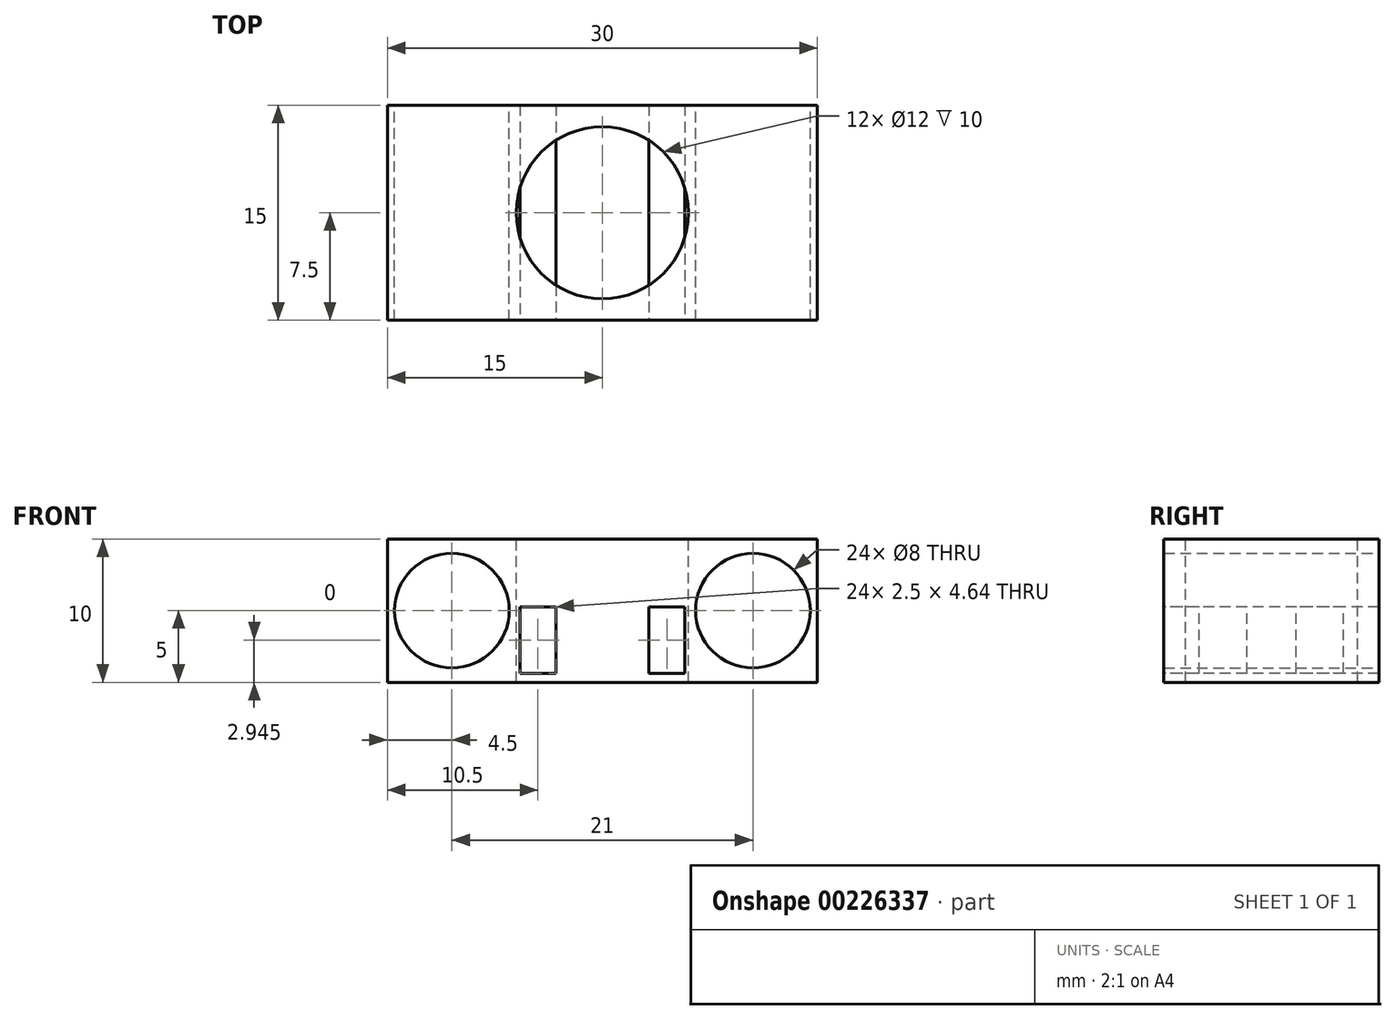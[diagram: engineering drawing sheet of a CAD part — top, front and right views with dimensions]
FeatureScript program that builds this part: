
annotation { "Feature Type Name" : "Feature", "Feature Type Description" : "" }
export const myFeature = defineFeature(function(context is Context, id is Id, definition is map)
    precondition{}
    {
        {
            var Q0;
            Q0=qCreatedBy(makeId("Front.planeOp"),FACE);
            var sketch = newSketch(context, id + "F0", { "sketchPlane" : qUnion([Q0])});
            skLineSegment(sketch, "E0.bottom", {"start": v(15, -5) * mm, "end": v(-15, -5) * mm});
            skLineSegment(sketch, "E0.top", {"start": v(15, 5) * mm, "end": v(-15, 5) * mm});
            skLineSegment(sketch, "E0.left", {"start": v(15, -5) * mm, "end": v(15, 5) * mm});
            skLineSegment(sketch, "E0.right", {"start": v(-15, -5) * mm, "end": v(-15, 5) * mm});
            skPoint(sketch, "E0.middle", {"position": v(0, 0) * mm});
            skCircle(sketch, "E1", {"center": v(10.5, 0) * mm, "radius": 4 * mm});
            skCircle(sketch, "E2", {"center": v(-10.5, 0) * mm, "radius": 4 * mm});
            skPoint(sketch, "E3.orphan", {"position": v(21, 0) * mm});
            skLineSegment(sketch, "E4", {"start": v(-10.5, 0) * mm, "end": v(-6.5, 0) * mm});
            skLineSegment(sketch, "E5", {"start": v(-6.5, 0) * mm, "end": v(0, 0) * mm});
            skLineSegment(sketch, "E6", {"start": v(0, 0) * mm, "end": v(6.5, 0) * mm});
            skLineSegment(sketch, "E7", {"start": v(6.5, 0) * mm, "end": v(10.05, 0) * mm});
            skLineSegment(sketch, "E8.bottom", {"start": v(6, -0.68) * mm, "end": v(-6, -0.68) * mm});
            skLineSegment(sketch, "E8.top", {"start": v(6, 0.68) * mm, "end": v(-6, 0.68) * mm});
            skLineSegment(sketch, "E8.left", {"start": v(6, -0.68) * mm, "end": v(6, 0.68) * mm});
            skLineSegment(sketch, "E8.right", {"start": v(-6, -0.68) * mm, "end": v(-6, 0.68) * mm});
            skSolve(sketch);
        }
        {
            var Q0;
            Q0 = qSketchRegion(id + "F0", true);
            var Q1;
            {var subQ1=sQuery(id+"F0.wireOp",EDGE,"E8.bottom");Q1=makeQuery(id+"F0.imprint","IMPRINT",FACE,{"disambiguationData":[TD([[makeQuery(id+"F0.imprint","IMPRINT",EDGE,{"derivedFrom":subQ1}),-1.0]])]});}
            var Q2;
            {var subQ1=sQuery(id+"F0.wireOp",EDGE,"E8.top");Q2=makeQuery(id+"F0.imprint","IMPRINT",FACE,{"disambiguationData":[TD([[makeQuery(id+"F0.imprint","IMPRINT",EDGE,{"derivedFrom":subQ1}),1.0]])]});}
            extrude(context, id + "F1", {"entities" : qUnion([Q0, Q1, Q2]), "depth" : 15 * mm});
        }
        {
            var Q0;
            Q0=makeQuery(id+"F1.opExtrude","SWEPT_FACE",FACE,{"disambiguationData":[OSD([sQuery(id+"F0.wireOp",EDGE,"E0.top")])]});
            var sketch = newSketch(context, id + "F2", { "sketchPlane" : qUnion([Q0])});
            skLineSegment(sketch, "E9", {"start": v(-15, -7.5) * mm, "end": v(15, -7.5) * mm});
            skCircle(sketch, "E10", {"center": v(0, -7.5) * mm, "radius": 6 * mm});
            skSolve(sketch);
        }
        {
            var Q0;
            Q0=sQuery(id+"F2.wireOp",VERTEX,"E10.center");
            var Q1;
            Q1=makeQuery(id+"F1.opExtrude","SWEPT_BODY",BODY,{"disambiguationData":[OSD([sQuery(id+"F0.wireOp",EDGE,"E0.bottom"),sQuery(id+"F0.wireOp",EDGE,"E0.top"),sQuery(id+"F0.wireOp",EDGE,"E0.left"),sQuery(id+"F0.wireOp",EDGE,"E0.right"),sQuery(id+"F0.wireOp",EDGE,"E1"),sQuery(id+"F0.wireOp",EDGE,"E2")])]});
            hole(context, id + "F3", {"style" : HoleStyle.SIMPLE, "endStyle" : HoleEndStyle.BLIND, "holeDiameter" : 12 * mm, "holeDepth" : 10 * mm, "locations" : qUnion([Q0]), "scope" : qUnion([Q1])});
        }
        {
            var Q0;
            Q0=makeQuery(id+"F1.opExtrude","CAP_FACE",FACE,{"disambiguationData":[OSD([sQuery(id+"F0.wireOp",EDGE,"E0.bottom"),sQuery(id+"F0.wireOp",EDGE,"E0.top"),sQuery(id+"F0.wireOp",EDGE,"E0.left"),sQuery(id+"F0.wireOp",EDGE,"E0.right"),sQuery(id+"F0.wireOp",EDGE,"E1"),sQuery(id+"F0.wireOp",EDGE,"E2")])],"isStart":false});
            var sketch = newSketch(context, id + "F4", { "sketchPlane" : qUnion([Q0])});
            skLineSegment(sketch, "E11.bottom", {"start": v(6, -5) * mm, "end": v(-6, -5) * mm});
            skLineSegment(sketch, "E11.top", {"start": v(6, 5) * mm, "end": v(-6, 5) * mm});
            skPoint(sketch, "E11.middle", {"position": v(0, 0) * mm});
            skLineSegment(sketch, "E12.bottom", {"start": v(3.25, -5) * mm, "end": v(-3.25, -5) * mm});
            skLineSegment(sketch, "E12.left", {"start": v(3.25, -5) * mm, "end": v(3.25, -2.5) * mm});
            skLineSegment(sketch, "E12.right", {"start": v(-3.25, -5) * mm, "end": v(-3.25, -2.5) * mm});
            skPoint(sketch, "E12.middle", {"position": v(0, -3.75) * mm});
            skLineSegment(sketch, "E13", {"start": v(-3.25, -3.75) * mm, "end": v(-3.25, -5) * mm});
            skLineSegment(sketch, "E14.bottom", {"start": v(-3.25, -4.37) * mm, "end": v(-5.75, -4.37) * mm});
            skLineSegment(sketch, "E14.top", {"start": v(-3.25, 0.26) * mm, "end": v(-5.75, 0.26) * mm});
            skLineSegment(sketch, "E14.left", {"start": v(-3.25, -4.37) * mm, "end": v(-3.25, 0.27) * mm});
            skLineSegment(sketch, "E14.right", {"start": v(-5.75, -4.38) * mm, "end": v(-5.75, 0.26) * mm});
            skLineSegment(sketch, "E15", {"start": v(3.25, -3.75) * mm, "end": v(3.25, -5) * mm});
            skLineSegment(sketch, "E16.bottom", {"start": v(3.25, -4.37) * mm, "end": v(5.75, -4.37) * mm});
            skLineSegment(sketch, "E16.top", {"start": v(3.25, 0.27) * mm, "end": v(5.75, 0.27) * mm});
            skLineSegment(sketch, "E16.left", {"start": v(3.25, -4.37) * mm, "end": v(3.25, 0.27) * mm});
            skLineSegment(sketch, "E16.right", {"start": v(5.75, -4.37) * mm, "end": v(5.75, 0.27) * mm});
            skSolve(sketch);
        }
        {
            var Q0;
            Q0 = qSketchRegion(id + "F4", true);
            extrude(context, id + "F5", {"entities" : qUnion([Q0]), "operationType" : NewBodyOperationType.REMOVE, "oppositeDirection" : true, "depth" : 25 * mm});
        }
        {
            var Q0;
            {var subQ3=sQuery(id+"F4.wireOp",EDGE,"E14.bottom");Q0=makeQuery(id+"F4.imprint","IMPRINT",FACE,{"disambiguationData":[TD([[makeQuery(id+"F4.imprint","IMPRINT",EDGE,{"derivedFrom":subQ3}),-1.0]])]});}
            var Q1;
            {var subQ3=sQuery(id+"F4.wireOp",EDGE,"E16.bottom");Q1=makeQuery(id+"F4.imprint","IMPRINT",FACE,{"disambiguationData":[TD([[makeQuery(id+"F4.imprint","IMPRINT",EDGE,{"derivedFrom":subQ3}),1.0]])]});}
            extrude(context, id + "F6", {"entities" : qUnion([Q0, Q1]), "oppositeDirection" : true, "depth" : 15 * mm});
        }
    });
